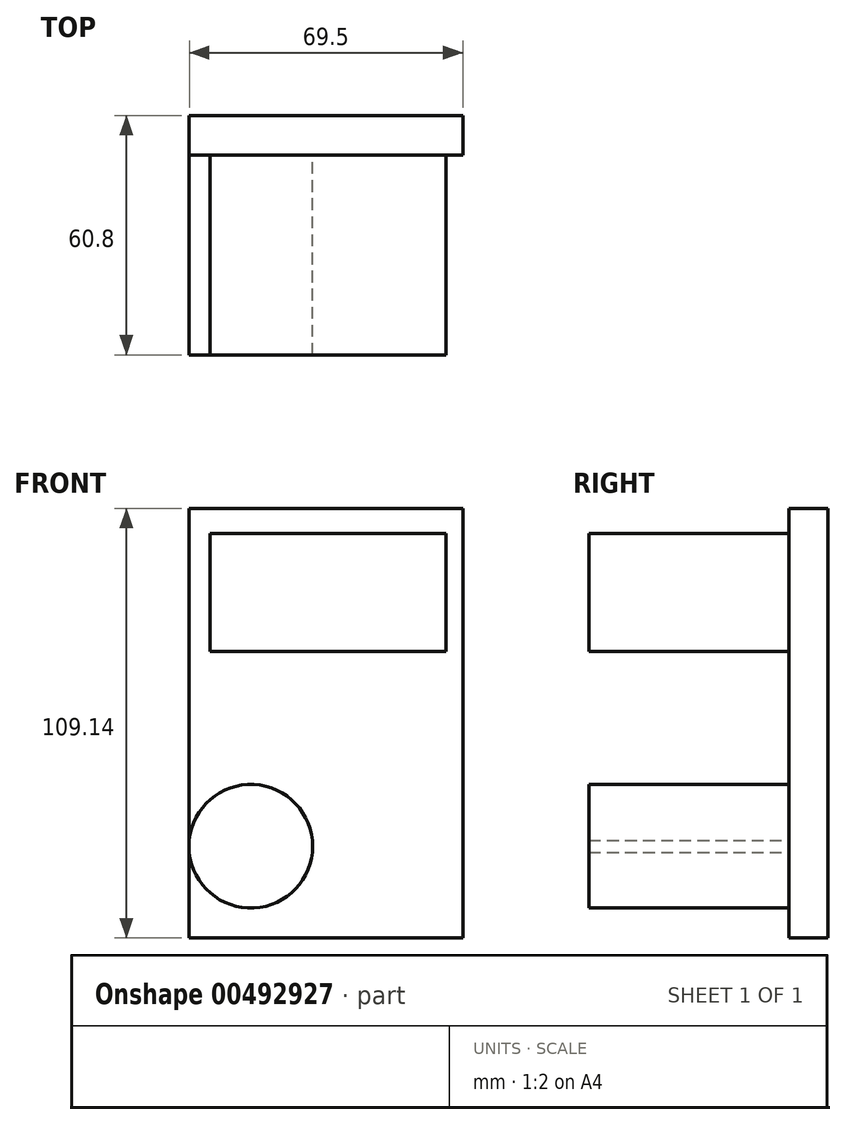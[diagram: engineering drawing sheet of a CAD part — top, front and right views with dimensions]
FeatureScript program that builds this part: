
annotation { "Feature Type Name" : "Feature", "Feature Type Description" : "" }
export const myFeature = defineFeature(function(context is Context, id is Id, definition is map)
    precondition{}
    {
        {
            var Q0;
            Q0=qCreatedBy(makeId("Front.planeOp"),FACE);
            var sketch = newSketch(context, id + "F0", { "sketchPlane" : qUnion([Q0])});
            skLineSegment(sketch, "E0.bottom", {"start": v(0, -35.4) * mm, "end": v(-69.5, -35.4) * mm});
            skLineSegment(sketch, "E0.top", {"start": v(0, 73.74) * mm, "end": v(-69.5, 73.74) * mm});
            skLineSegment(sketch, "E0.left", {"start": v(0, -35.4) * mm, "end": v(0, 73.74) * mm});
            skLineSegment(sketch, "E0.right", {"start": v(-69.5, -35.4) * mm, "end": v(-69.5, 73.74) * mm});
            skSolve(sketch);
        }
        {
            var Q0;
            Q0 = qSketchRegion(id + "F0", true);
            extrude(context, id + "F1", {"entities" : qUnion([Q0]), "depth" : 10 * mm});
        }
        {
            var Q0;
            Q0=makeQuery(id+"F1.opExtrude","CAP_FACE",FACE,{"disambiguationData":[OSD([sQuery(id+"F0.wireOp",EDGE,"E0.bottom"),sQuery(id+"F0.wireOp",EDGE,"E0.top"),sQuery(id+"F0.wireOp",EDGE,"E0.left"),sQuery(id+"F0.wireOp",EDGE,"E0.right")])],"isStart":false});
            var sketch = newSketch(context, id + "F2", { "sketchPlane" : qUnion([Q0])});
            skLineSegment(sketch, "E1.bottom", {"start": v(-64.28, 37.38) * mm, "end": v(-4.28, 37.38) * mm});
            skLineSegment(sketch, "E1.top", {"start": v(-64.28, 67.38) * mm, "end": v(-4.28, 67.38) * mm});
            skLineSegment(sketch, "E1.left", {"start": v(-64.28, 37.38) * mm, "end": v(-64.28, 67.38) * mm});
            skLineSegment(sketch, "E1.right", {"start": v(-4.28, 37.38) * mm, "end": v(-4.28, 67.38) * mm});
            skSolve(sketch);
        }
        {
            var Q0;
            Q0=makeQuery(id+"F2.imprint","IMPRINT",FACE,{"disambiguationData":[TD([[makeQuery(id+"F2.imprint","IMPRINT",EDGE,{"derivedFrom":sQuery(id+"F2.wireOp",EDGE,"E1.bottom")}),-1.0]])]});
            var sketch = newSketch(context, id + "F3", { "sketchPlane" : qUnion([Q0])});
            skCircle(sketch, "E2", {"center": v(-53.88, -12.12) * mm, "radius": 15.7 * mm});
            skSolve(sketch);
        }
        {
            var Q0;
            Q0=makeQuery(id+"F2.imprint","IMPRINT",FACE,{"disambiguationData":[TD([[makeQuery(id+"F2.imprint","IMPRINT",EDGE,{"derivedFrom":sQuery(id+"F2.wireOp",EDGE,"E1.bottom")}),1.0]])]});
            extrude(context, id + "F4", {"entities" : qUnion([Q0]), "operationType" : NewBodyOperationType.ADD, "depth" : 50.8 * mm});
        }
        {
            var Q0;
            {var subQ0=sQuery(id+"F3.wireOp",EDGE,"E2");var subQ1=makeQuery(id+"F2.imprint","IMPRINT",EDGE,{"derivedFrom":makeQuery(id+"F1.opExtrude","CAP_EDGE",EDGE,{"disambiguationData":[OSD([sQuery(id+"F0.wireOp",EDGE,"E0.right")])],"isStart":false})});var subQ2=makeQuery(id+"F3.imprint","INTERSECT",VERTEX,{"disambiguationData":[OD(0.0)],"derivedFrom":[subQ1,subQ0]});Q0=makeQuery(id+"F3.imprint","IMPRINT",FACE,{"disambiguationData":[TD([[makeQuery(id+"F3.imprint","IMPRINT",EDGE,{"disambiguationData":[TD([[subQ2,-1.0]])],"derivedFrom":subQ0}),1.0]])]});}
            extrude(context, id + "F5", {"entities" : qUnion([Q0]), "operationType" : NewBodyOperationType.ADD, "depth" : 50.8 * mm});
        }
    });
